# Revit family: Konsole 45- 45 Platte längs VA
name_source: partatom
category: HLS-Bauteile
revit_build: Autodesk Revit 2017 (Build: 20190508_0315(x64)
units: mm (PartAtom-declared; Revit-internal decimal feet)

## family parameters
Basisbauteil = Fläche
Beim Laden mit Abzugskörper schneiden = Nein
Bemaßung runder Anschluss = Durchmesser verwenden
Gemeinsam genutzt = Ja
Raumberechnungspunkt = Nein
Teiletyp = Normal

## types (8) — shared parameters
Ausrichtung Platte = längs
Breite Platte = 50 mm  [stored 0.164042 ft]
Breite Profil = 45 mm  [stored 0.147638 ft]
Fabrikat = MEFA
Firma = MEFA Befestigungs- und Montagesysteme GmbH
Höhe Profil = 45 mm  [stored 0.147638 ft]
Langloch Platte = val.LanglochPlatte.13x20 mm
Lochabstand = 85 mm
Länge Platte = 127 mm
Material = Edelstahl
Profil = C-Profil
Stärke Platte = 8 mm  [stored 0.0262467 ft]
Stärke Profil = 2 mm  [stored 0.00656168 ft]
Vorgabe-Ansicht = 1219 mm

## per-type parameters (varying)
| type | Artikelnummer | EAN | Gewicht | Kurztext1 | Kurztext2 | Länge Konsole | Schienenlänge | max. zul. Last F1 | max. zul. Last F2 | max. zul. Last q0 |
| Konsole 45- 45 L= 525 Platte längs V4A | 0481664 | 4250928459152 | 1.70 kg | Konsole C-Profil 45/45 V4A | L= 525 mm Platte längs | 525 mm | Montageschiene 45- 45-2,0 für Konsole VA : C-Profil 45- 45-2,0 L= 525 V4A | 0.30 kip | 0.15 kip | 0.175 kip/ft |
| Konsole 45- 45 L= 525 Platte längs V2A | 0480664 | 4250928459190 | 1.70 kg | Konsole C-Profil 45/45 V2A | L= 525 mm Platte längs | 525 mm | Montageschiene 45- 45-2,0 für Konsole VA : C-Profil 45- 45-2,0 L= 525 V2A | 0.25 kip | 0.13 kip | 0.147 kip/ft |
| Konsole 45- 45 L= 420 Platte längs V2A | 0480663 | 4250928459183 | 1.44 kg | Konsole C-Profil 45/45 V2A | L= 420 mm Platte längs | 420 mm  [stored 1.37795 ft] | Montageschiene 45- 45-2,0 für Konsole VA : C-Profil 45- 45-2,0 L= 420 V2A | 0.31 kip | 0.16 kip | 0.229 kip/ft |
| Konsole 45- 45 L= 315 Platte längs V4A | 0481662 | 4250928459138 | 1.18 kg | Konsole C-Profil 45/45 V4A | L= 315 mm Platte längs | 315 mm  [stored 1.03346 ft] | Montageschiene 45- 45-2,0 für Konsole VA : C-Profil 45- 45-2,0 L= 315 V4A | 0.50 kip | 0.25 kip | 0.488 kip/ft |
| Konsole 45- 45 L= 315 Platte längs V2A | 0480662 | 4250928459176 | 1.18 kg | Konsole C-Profil 45/45 V2A | L= 315 mm Platte längs | 315 mm  [stored 1.03346 ft] | Montageschiene 45- 45-2,0 für Konsole VA : C-Profil 45- 45-2,0 L= 315 V2A | 0.42 kip | 0.21 kip | 0.406 kip/ft |
| Konsole 45- 45 L= 210 Platte längs V2A | 0480661 | 4250928459169 | 0.92 kg | Konsole C-Profil 45/45 V2A | L= 210 mm Platte längs | 210 mm  [stored 0.688976 ft] | Montageschiene 45- 45-2,0 für Konsole VA : C-Profil 45- 45-2,0 L= 210 V2A | 0.63 kip | 0.31 kip | 0.915 kip/ft |
| Konsole 45- 45 L= 210 Platte längs V4A | 0481661 | 4250928459121 | 0.92 kg | Konsole C-Profil 45/45 V4A | L= 210 mm Platte längs | 210 mm  [stored 0.688976 ft] | Montageschiene 45- 45-2,0 für Konsole VA : C-Profil 45- 45-2,0 L= 210 V4A | 0.76 kip | 0.38 kip | 1.098 kip/ft |
| Konsole 45- 45 L= 420 Platte längs V4A | 0481663 | 4250928459145 | 1.44 kg | Konsole C-Profil 45/45 V4A | L= 420 mm Platte längs | 420 mm  [stored 1.37795 ft] | Montageschiene 45- 45-2,0 für Konsole VA : C-Profil 45- 45-2,0 L= 420 V4A | 0.38 kip | 0.19 kip | 0.275 kip/ft |

note: [stored X ft] marks values corroborated as IEEE doubles in the binary element streams (Revit-internal decimal feet)
